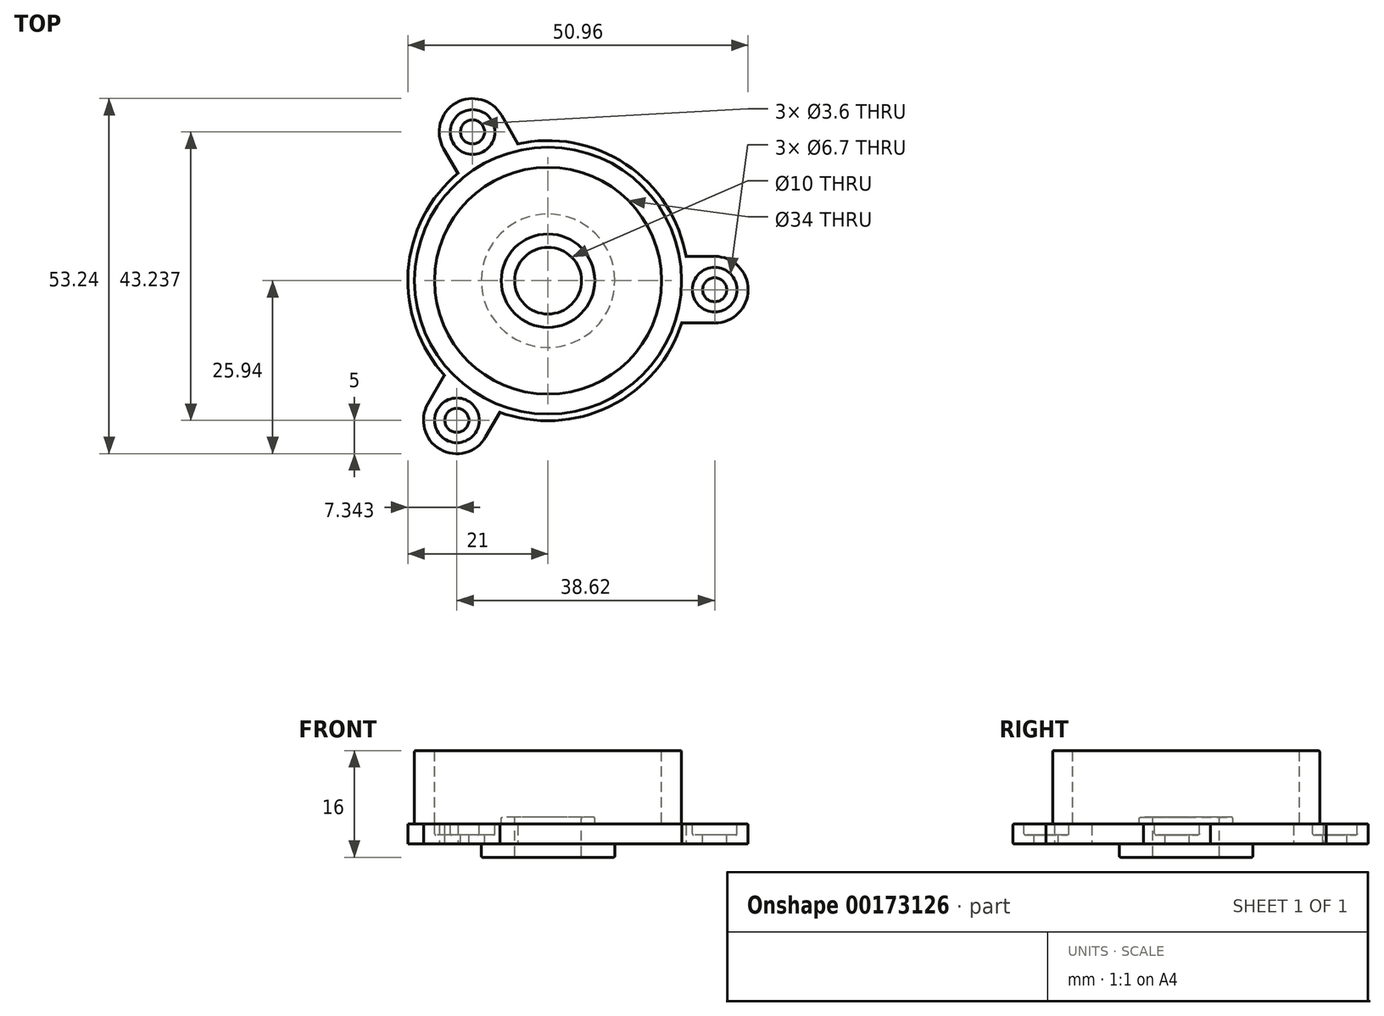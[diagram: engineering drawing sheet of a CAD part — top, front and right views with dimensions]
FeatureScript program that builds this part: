
annotation { "Feature Type Name" : "Feature", "Feature Type Description" : "" }
export const myFeature = defineFeature(function(context is Context, id is Id, definition is map)
    precondition{}
    {
        {
            var Q0;
            Q0=qCreatedBy(makeId("Front.planeOp"),FACE);
            var sketch = newSketch(context, id + "F0", { "sketchPlane" : qUnion([Q0])});
            skLineSegment(sketch, "E0", {"start": v(7, 0) * mm, "end": v(17, 0) * mm});
            skLineSegment(sketch, "E1", {"start": v(17, 0) * mm, "end": v(17, 11) * mm});
            skLineSegment(sketch, "E2", {"start": v(17, 11) * mm, "end": v(20, 11) * mm});
            skLineSegment(sketch, "E3", {"start": v(20, 11) * mm, "end": v(20, 0) * mm});
            skLineSegment(sketch, "E4", {"start": v(20, 0) * mm, "end": v(21, 0) * mm});
            skLineSegment(sketch, "E5", {"start": v(21, 0) * mm, "end": v(21, -3) * mm});
            skLineSegment(sketch, "E6", {"start": v(21, -3) * mm, "end": v(10, -3) * mm});
            skLineSegment(sketch, "E7", {"start": v(10, -3) * mm, "end": v(10, -5) * mm});
            skLineSegment(sketch, "E8", {"start": v(10, -5) * mm, "end": v(5, -5) * mm});
            skLineSegment(sketch, "E9", {"start": v(5, -5) * mm, "end": v(5, 0) * mm});
            skLineSegment(sketch, "E10", {"start": v(5, 0) * mm, "end": v(5, 1) * mm});
            skLineSegment(sketch, "E11", {"start": v(5, 1) * mm, "end": v(7, 1) * mm});
            skLineSegment(sketch, "E12", {"start": v(7, 1) * mm, "end": v(7, 0) * mm});
            skSolve(sketch);
        }
        {
            var Q0;
            Q0=qCreatedBy(makeId("Front.planeOp"),FACE);
            var sketch = newSketch(context, id + "F1", { "sketchPlane" : qUnion([Q0])});
            skLineSegment(sketch, "E13", {"start": v(0, 12.54) * mm, "end": v(0, -18) * mm});
            skSolve(sketch);
        }
        {
            var Q0;
            Q0=makeQuery(id+"F0.imprint","IMPRINT",FACE,{"disambiguationData":[TD([[makeQuery(id+"F0.imprint","IMPRINT",EDGE,{"derivedFrom":sQuery(id+"F0.wireOp",EDGE,"E0")}),-1.0]])]});
            var Q1;
            Q1=sQuery(id+"F1.wireOp",EDGE,"E13");
            revolve(context, id + "F2", {"entities" : qUnion([Q0]), "axis" : qUnion([Q1]), "revolveType" : RevolveType.FULL});
        }
        {
            var Q0;
            Q0=makeQuery(id+"F2.opRevolve","SWEPT_FACE",FACE,{"disambiguationData":[OSD([sQuery(id+"F0.wireOp",EDGE,"E6")])]});
            var sketch = newSketch(context, id + "F3", { "sketchPlane" : qUnion([Q0])});
            skArc(sketch, "E14", {"start": v(24.96, -3.64) * mm, "mid": v(29.96, 1.36) * mm, "end": v(24.96, 6.36) * mm});
            skLineSegment(sketch, "E15", {"start": v(24.96, 6.36) * mm, "end": v(20.01, 6.36) * mm});
            skLineSegment(sketch, "E16", {"start": v(24.96, -3.64) * mm, "end": v(20.68, -3.64) * mm});
            skLineSegment(sketch, "E17.1.0", {"start": v(-17.99, 18.44) * mm, "end": v(-15.51, 14.15) * mm});
            skArc(sketch, "E17.1.1", {"start": v(-9.33, 23.44) * mm, "mid": v(-16.16, 25.27) * mm, "end": v(-17.99, 18.44) * mm});
            skLineSegment(sketch, "E17.1.2", {"start": v(-9.33, 23.44) * mm, "end": v(-7.19, 19.73) * mm});
            skLineSegment(sketch, "E17.2.0", {"start": v(-6.98, -24.8) * mm, "end": v(-4.5, -20.51) * mm});
            skArc(sketch, "E17.2.1", {"start": v(-15.64, -19.8) * mm, "mid": v(-13.8, -26.63) * mm, "end": v(-6.98, -24.8) * mm});
            skLineSegment(sketch, "E17.2.2", {"start": v(-15.64, -19.8) * mm, "end": v(-13.5, -16.09) * mm});
            skPoint(sketch, "E17.center", {"position": v(0, 0) * mm});
            skSolve(sketch);
        }
        {
            var Q0;
            Q0=makeQuery(id+"F3.imprint","IMPRINT",FACE,{"disambiguationData":[TD([[makeQuery(id+"F3.imprint","IMPRINT",EDGE,{"derivedFrom":sQuery(id+"F3.wireOp",EDGE,"E14")}),1.0]])]});
            var Q1;
            {var subQ0=sQuery(id+"F3.wireOp",EDGE,"E17.1.0");Q1=makeQuery(id+"F3.imprint","IMPRINT",FACE,{"disambiguationData":[TD([[makeQuery(id+"F3.imprint","IMPRINT",EDGE,{"derivedFrom":subQ0}),1.0]])]});}
            var Q2;
            {var subQ0=sQuery(id+"F3.wireOp",EDGE,"E17.2.0");Q2=makeQuery(id+"F3.imprint","IMPRINT",FACE,{"disambiguationData":[TD([[makeQuery(id+"F3.imprint","IMPRINT",EDGE,{"derivedFrom":subQ0}),1.0]])]});}
            extrude(context, id + "F4", {"entities" : qUnion([Q0, Q1, Q2]), "operationType" : NewBodyOperationType.ADD, "oppositeDirection" : true, "depth" : 3 * mm});
        }
        {
            var Q0;
            {var subQ0=sQuery(id+"F0.wireOp",EDGE,"E6");var subQ1=sQuery(id+"F0.wireOp",EDGE,"E5");Q0=makeQuery(id+"F4.boolean.opBoolean","MERGE",FACE,{"derivedFrom":[makeQuery(id+"F2.opRevolve","SWEPT_FACE",FACE,{"disambiguationData":[OSD([sQuery(id+"F0.wireOp",EDGE,"E4")])]}),makeQuery(id+"F4.opExtrude","CAP_FACE",FACE,{"disambiguationData":[OSD([subQ1,subQ0,sQuery(id+"F3.wireOp",EDGE,"E14"),sQuery(id+"F3.wireOp",EDGE,"E15"),sQuery(id+"F3.wireOp",EDGE,"E16")])],"isStart":false}),makeQuery(id+"F4.opExtrude","CAP_FACE",FACE,{"disambiguationData":[OSD([subQ1,subQ0,sQuery(id+"F3.wireOp",EDGE,"E17.1.0"),sQuery(id+"F3.wireOp",EDGE,"E17.1.1"),sQuery(id+"F3.wireOp",EDGE,"E17.1.2")])],"isStart":false}),makeQuery(id+"F4.opExtrude","CAP_FACE",FACE,{"disambiguationData":[OSD([subQ1,subQ0,sQuery(id+"F3.wireOp",EDGE,"E17.2.0"),sQuery(id+"F3.wireOp",EDGE,"E17.2.1"),sQuery(id+"F3.wireOp",EDGE,"E17.2.2")])],"isStart":false})]});}
            var sketch = newSketch(context, id + "F5", { "sketchPlane" : qUnion([Q0])});
            skCircle(sketch, "E18", {"center": v(-13.66, -20.94) * mm, "radius": 1.8 * mm});
            skCircle(sketch, "E19.1.0", {"center": v(24.96, -1.36) * mm, "radius": 1.8 * mm});
            skCircle(sketch, "E19.2.0", {"center": v(-11.3, 22.3) * mm, "radius": 1.8 * mm});
            skPoint(sketch, "E19.center", {"position": v(0, 0) * mm});
            skSolve(sketch);
        }
        {
            var Q0;
            Q0=makeQuery(id+"F5.imprint","IMPRINT",FACE,{"disambiguationData":[TD([[makeQuery(id+"F5.imprint","IMPRINT",EDGE,{"derivedFrom":sQuery(id+"F5.wireOp",EDGE,"E18")}),1.0]])]});
            var Q1;
            Q1=makeQuery(id+"F5.imprint","IMPRINT",FACE,{"disambiguationData":[TD([[makeQuery(id+"F5.imprint","IMPRINT",EDGE,{"derivedFrom":sQuery(id+"F5.wireOp",EDGE,"E19.1.0")}),1.0]])]});
            var Q2;
            Q2=makeQuery(id+"F5.imprint","IMPRINT",FACE,{"disambiguationData":[TD([[makeQuery(id+"F5.imprint","IMPRINT",EDGE,{"derivedFrom":sQuery(id+"F5.wireOp",EDGE,"E19.2.0")}),1.0]])]});
            extrude(context, id + "F6", {"entities" : qUnion([Q0, Q1, Q2]), "operationType" : NewBodyOperationType.REMOVE, "endBound" : BoundingType.THROUGH_ALL, "oppositeDirection" : true, "depth" : 25 * mm});
        }
        {
            var Q0;
            {var subQ0=sQuery(id+"F0.wireOp",EDGE,"E6");var subQ1=sQuery(id+"F0.wireOp",EDGE,"E5");Q0=makeQuery(id+"F4.boolean.opBoolean","MERGE",FACE,{"derivedFrom":[makeQuery(id+"F2.opRevolve","SWEPT_FACE",FACE,{"disambiguationData":[OSD([sQuery(id+"F0.wireOp",EDGE,"E4")])]}),makeQuery(id+"F4.opExtrude","CAP_FACE",FACE,{"disambiguationData":[OSD([subQ1,subQ0,sQuery(id+"F3.wireOp",EDGE,"E14"),sQuery(id+"F3.wireOp",EDGE,"E15"),sQuery(id+"F3.wireOp",EDGE,"E16")])],"isStart":false}),makeQuery(id+"F4.opExtrude","CAP_FACE",FACE,{"disambiguationData":[OSD([subQ1,subQ0,sQuery(id+"F3.wireOp",EDGE,"E17.1.0"),sQuery(id+"F3.wireOp",EDGE,"E17.1.1"),sQuery(id+"F3.wireOp",EDGE,"E17.1.2")])],"isStart":false}),makeQuery(id+"F4.opExtrude","CAP_FACE",FACE,{"disambiguationData":[OSD([subQ1,subQ0,sQuery(id+"F3.wireOp",EDGE,"E17.2.0"),sQuery(id+"F3.wireOp",EDGE,"E17.2.1"),sQuery(id+"F3.wireOp",EDGE,"E17.2.2")])],"isStart":false})]});}
            var sketch = newSketch(context, id + "F7", { "sketchPlane" : qUnion([Q0])});
            skCircle(sketch, "E20", {"center": v(-13.66, -20.94) * mm, "radius": 3.35 * mm});
            skCircle(sketch, "E21.1.0", {"center": v(24.96, -1.36) * mm, "radius": 3.35 * mm});
            skCircle(sketch, "E21.2.0", {"center": v(-11.3, 22.3) * mm, "radius": 3.35 * mm});
            skPoint(sketch, "E21.center", {"position": v(0, 0) * mm});
            skSolve(sketch);
        }
        {
            var Q0;
            Q0=makeQuery(id+"F7.imprint","IMPRINT",FACE,{"disambiguationData":[TD([[makeQuery(id+"F7.imprint","IMPRINT",EDGE,{"derivedFrom":sQuery(id+"F7.wireOp",EDGE,"E20")}),1.0]])]});
            var Q1;
            Q1=makeQuery(id+"F7.imprint","IMPRINT",FACE,{"disambiguationData":[TD([[makeQuery(id+"F7.imprint","IMPRINT",EDGE,{"derivedFrom":sQuery(id+"F7.wireOp",EDGE,"E21.1.0")}),1.0]])]});
            var Q2;
            Q2=makeQuery(id+"F7.imprint","IMPRINT",FACE,{"disambiguationData":[TD([[makeQuery(id+"F7.imprint","IMPRINT",EDGE,{"derivedFrom":sQuery(id+"F7.wireOp",EDGE,"E21.2.0")}),1.0]])]});
            extrude(context, id + "F8", {"entities" : qUnion([Q0, Q1, Q2]), "operationType" : NewBodyOperationType.REMOVE, "oppositeDirection" : true, "depth" : 1.65 * mm});
        }
        {
            var Q0;
            Q0=makeQuery(id+"F2.opRevolve","SWEPT_EDGE",EDGE,{"disambiguationData":[OSD([sQuery(id+"F0.wireOp",EDGE,"E1"),sQuery(id+"F0.wireOp",EDGE,"E2")])]});
            var Q1;
            Q1=makeQuery(id+"F2.opRevolve","SWEPT_EDGE",EDGE,{"disambiguationData":[OSD([sQuery(id+"F0.wireOp",EDGE,"E2"),sQuery(id+"F0.wireOp",EDGE,"E3")])]});
            var Q2;
            Q2=makeQuery(id+"F2.opRevolve","SWEPT_EDGE",EDGE,{"disambiguationData":[OSD([sQuery(id+"F0.wireOp",EDGE,"E0"),sQuery(id+"F0.wireOp",EDGE,"E1")])]});
            var Q3;
            Q3=makeQuery(id+"F2.opRevolve","SWEPT_EDGE",EDGE,{"disambiguationData":[OSD([sQuery(id+"F0.wireOp",EDGE,"E11"),sQuery(id+"F0.wireOp",EDGE,"E12")])]});
            var Q4;
            Q4=makeQuery(id+"F2.opRevolve","SWEPT_EDGE",EDGE,{"disambiguationData":[OSD([sQuery(id+"F0.wireOp",EDGE,"E10"),sQuery(id+"F0.wireOp",EDGE,"E11")])]});
            var Q5;
            Q5=makeQuery(id+"F2.opRevolve","SWEPT_EDGE",EDGE,{"disambiguationData":[OSD([sQuery(id+"F0.wireOp",EDGE,"E0"),sQuery(id+"F0.wireOp",EDGE,"E12")])]});
            var Q6;
            {var subQ0=sQuery(id+"F3.wireOp",EDGE,"E16");var subQ1=sQuery(id+"F0.wireOp",EDGE,"E4");var subQ3=sQuery(id+"F0.wireOp",EDGE,"E5");Q6=makeQuery(id+"F4.boolean.opBoolean","SPLIT",EDGE,{"disambiguationData":[TD([makeQuery(id+"F4.opExtrude","SWEPT_FACE",FACE,{"disambiguationData":[OSD([subQ0])]})])],"derivedFrom":makeQuery(id+"F2.opRevolve","SWEPT_EDGE",EDGE,{"disambiguationData":[OSD([subQ1,subQ3])]})});}
            var Q7;
            Q7=makeQuery(id+"F2.opRevolve","SWEPT_EDGE",EDGE,{"disambiguationData":[OSD([sQuery(id+"F0.wireOp",EDGE,"E3"),sQuery(id+"F0.wireOp",EDGE,"E4")])]});
            var Q8;
            Q8=makeQuery(id+"F4.opExtrude","CAP_EDGE",EDGE,{"disambiguationData":[OSD([sQuery(id+"F3.wireOp",EDGE,"E17.2.0")])],"isStart":false});
            var Q9;
            Q9=makeQuery(id+"F4.opExtrude","CAP_EDGE",EDGE,{"disambiguationData":[OSD([sQuery(id+"F3.wireOp",EDGE,"E17.2.1")])],"isStart":false});
            var Q10;
            Q10=makeQuery(id+"F4.opExtrude","CAP_EDGE",EDGE,{"disambiguationData":[OSD([sQuery(id+"F3.wireOp",EDGE,"E17.2.2")])],"isStart":false});
            var Q11;
            Q11=makeQuery(id+"F8.boolean.opBoolean","COPY",EDGE,{"derivedFrom":makeQuery(id+"F8.opExtrude","CAP_EDGE",EDGE,{"disambiguationData":[OSD([sQuery(id+"F7.wireOp",EDGE,"E21.2.0")])],"isStart":true})});
            var Q12;
            Q12=makeQuery(id+"F8.boolean.opBoolean","COPY",EDGE,{"derivedFrom":makeQuery(id+"F8.opExtrude","CAP_EDGE",EDGE,{"disambiguationData":[OSD([sQuery(id+"F7.wireOp",EDGE,"E21.2.0")])],"isStart":false})});
            var Q13;
            Q13=makeQuery(id+"F8.boolean.opBoolean","COPY",EDGE,{"derivedFrom":makeQuery(id+"F8.opExtrude","CAP_EDGE",EDGE,{"disambiguationData":[OSD([sQuery(id+"F5.wireOp",EDGE,"E19.2.0")])],"isStart":false})});
            var Q14;
            {var subQ0=sQuery(id+"F0.wireOp",EDGE,"E6");var subQ1=sQuery(id+"F0.wireOp",EDGE,"E5");Q14=makeQuery(id+"F6.boolean.opBoolean","INTERSECT",EDGE,{"derivedFrom":[makeQuery(id+"F4.boolean.opBoolean","MERGE",FACE,{"derivedFrom":[makeQuery(id+"F2.opRevolve","SWEPT_FACE",FACE,{"disambiguationData":[OSD([subQ0])]}),makeQuery(id+"F4.opExtrude","CAP_FACE",FACE,{"disambiguationData":[OSD([subQ1,subQ0,sQuery(id+"F3.wireOp",EDGE,"E14"),sQuery(id+"F3.wireOp",EDGE,"E15"),sQuery(id+"F3.wireOp",EDGE,"E16")])],"isStart":true}),makeQuery(id+"F4.opExtrude","CAP_FACE",FACE,{"disambiguationData":[OSD([subQ1,subQ0,sQuery(id+"F3.wireOp",EDGE,"E17.1.0"),sQuery(id+"F3.wireOp",EDGE,"E17.1.1"),sQuery(id+"F3.wireOp",EDGE,"E17.1.2")])],"isStart":true}),makeQuery(id+"F4.opExtrude","CAP_FACE",FACE,{"disambiguationData":[OSD([subQ1,subQ0,sQuery(id+"F3.wireOp",EDGE,"E17.2.0"),sQuery(id+"F3.wireOp",EDGE,"E17.2.1"),sQuery(id+"F3.wireOp",EDGE,"E17.2.2")])],"isStart":true})]}),makeQuery(id+"F6.opExtrude","SWEPT_FACE",FACE,{"disambiguationData":[OSD([sQuery(id+"F5.wireOp",EDGE,"E19.2.0")])]})]});}
            var Q15;
            Q15=makeQuery(id+"F4.opExtrude","CAP_EDGE",EDGE,{"disambiguationData":[OSD([sQuery(id+"F3.wireOp",EDGE,"E17.2.0")])],"isStart":true});
            var Q16;
            Q16=makeQuery(id+"F4.opExtrude","CAP_EDGE",EDGE,{"disambiguationData":[OSD([sQuery(id+"F3.wireOp",EDGE,"E17.2.1")])],"isStart":true});
            var Q17;
            Q17=makeQuery(id+"F4.opExtrude","CAP_EDGE",EDGE,{"disambiguationData":[OSD([sQuery(id+"F3.wireOp",EDGE,"E17.2.1")])],"isStart":true});
            var Q18;
            {var subQ0=sQuery(id+"F3.wireOp",EDGE,"E16");var subQ1=sQuery(id+"F0.wireOp",EDGE,"E6");var subQ2=sQuery(id+"F0.wireOp",EDGE,"E5");Q18=makeQuery(id+"F4.boolean.opBoolean","SPLIT",EDGE,{"disambiguationData":[TD([makeQuery(id+"F4.opExtrude","SWEPT_FACE",FACE,{"disambiguationData":[OSD([subQ0])]})])],"derivedFrom":makeQuery(id+"F2.opRevolve","SWEPT_EDGE",EDGE,{"disambiguationData":[OSD([subQ2,subQ1])]})});}
            var Q19;
            Q19=makeQuery(id+"F4.opExtrude","CAP_EDGE",EDGE,{"disambiguationData":[OSD([sQuery(id+"F3.wireOp",EDGE,"E16")])],"isStart":false});
            var Q20;
            Q20=makeQuery(id+"F8.boolean.opBoolean","COPY",EDGE,{"derivedFrom":makeQuery(id+"F8.opExtrude","CAP_EDGE",EDGE,{"disambiguationData":[OSD([sQuery(id+"F7.wireOp",EDGE,"E21.1.0")])],"isStart":true})});
            var Q21;
            Q21=makeQuery(id+"F8.boolean.opBoolean","COPY",EDGE,{"derivedFrom":makeQuery(id+"F8.opExtrude","CAP_EDGE",EDGE,{"disambiguationData":[OSD([sQuery(id+"F7.wireOp",EDGE,"E21.1.0")])],"isStart":false})});
            var Q22;
            {var subQ0=sQuery(id+"F0.wireOp",EDGE,"E6");var subQ1=sQuery(id+"F0.wireOp",EDGE,"E5");Q22=makeQuery(id+"F6.boolean.opBoolean","INTERSECT",EDGE,{"derivedFrom":[makeQuery(id+"F4.boolean.opBoolean","MERGE",FACE,{"derivedFrom":[makeQuery(id+"F2.opRevolve","SWEPT_FACE",FACE,{"disambiguationData":[OSD([subQ0])]}),makeQuery(id+"F4.opExtrude","CAP_FACE",FACE,{"disambiguationData":[OSD([subQ1,subQ0,sQuery(id+"F3.wireOp",EDGE,"E14"),sQuery(id+"F3.wireOp",EDGE,"E15"),sQuery(id+"F3.wireOp",EDGE,"E16")])],"isStart":true}),makeQuery(id+"F4.opExtrude","CAP_FACE",FACE,{"disambiguationData":[OSD([subQ1,subQ0,sQuery(id+"F3.wireOp",EDGE,"E17.1.0"),sQuery(id+"F3.wireOp",EDGE,"E17.1.1"),sQuery(id+"F3.wireOp",EDGE,"E17.1.2")])],"isStart":true}),makeQuery(id+"F4.opExtrude","CAP_FACE",FACE,{"disambiguationData":[OSD([subQ1,subQ0,sQuery(id+"F3.wireOp",EDGE,"E17.2.0"),sQuery(id+"F3.wireOp",EDGE,"E17.2.1"),sQuery(id+"F3.wireOp",EDGE,"E17.2.2")])],"isStart":true})]}),makeQuery(id+"F6.opExtrude","SWEPT_FACE",FACE,{"disambiguationData":[OSD([sQuery(id+"F5.wireOp",EDGE,"E19.1.0")])]})]});}
            var Q23;
            Q23=makeQuery(id+"F8.boolean.opBoolean","COPY",EDGE,{"derivedFrom":makeQuery(id+"F8.opExtrude","CAP_EDGE",EDGE,{"disambiguationData":[OSD([sQuery(id+"F5.wireOp",EDGE,"E19.1.0")])],"isStart":false})});
            var Q24;
            Q24=makeQuery(id+"F4.opExtrude","CAP_EDGE",EDGE,{"disambiguationData":[OSD([sQuery(id+"F3.wireOp",EDGE,"E15")])],"isStart":false});
            var Q25;
            Q25=makeQuery(id+"F4.opExtrude","CAP_EDGE",EDGE,{"disambiguationData":[OSD([sQuery(id+"F3.wireOp",EDGE,"E14")])],"isStart":false});
            var Q26;
            {var subQ0=sQuery(id+"F3.wireOp",EDGE,"E15");var subQ3=sQuery(id+"F0.wireOp",EDGE,"E5");var subQ4=sQuery(id+"F0.wireOp",EDGE,"E4");Q26=makeQuery(id+"F4.boolean.opBoolean","SPLIT",EDGE,{"disambiguationData":[TD([makeQuery(id+"F4.opExtrude","SWEPT_FACE",FACE,{"disambiguationData":[OSD([subQ0])]})])],"derivedFrom":makeQuery(id+"F2.opRevolve","SWEPT_EDGE",EDGE,{"disambiguationData":[OSD([subQ4,subQ3])]})});}
            var Q27;
            Q27=makeQuery(id+"F4.opExtrude","CAP_EDGE",EDGE,{"disambiguationData":[OSD([sQuery(id+"F3.wireOp",EDGE,"E17.1.2")])],"isStart":false});
            var Q28;
            {var subQ0=sQuery(id+"F3.wireOp",EDGE,"E15");var subQ2=sQuery(id+"F0.wireOp",EDGE,"E6");var subQ3=sQuery(id+"F0.wireOp",EDGE,"E5");Q28=makeQuery(id+"F4.boolean.opBoolean","SPLIT",EDGE,{"disambiguationData":[TD([makeQuery(id+"F4.opExtrude","SWEPT_FACE",FACE,{"disambiguationData":[OSD([subQ0])]})])],"derivedFrom":makeQuery(id+"F2.opRevolve","SWEPT_EDGE",EDGE,{"disambiguationData":[OSD([subQ3,subQ2])]})});}
            var Q29;
            Q29=makeQuery(id+"F4.opExtrude","SWEPT_EDGE",EDGE,{"disambiguationData":[OSD([sQuery(id+"F0.wireOp",EDGE,"E5"),sQuery(id+"F0.wireOp",EDGE,"E6"),sQuery(id+"F3.wireOp",EDGE,"E17.1.2")])]});
            var Q30;
            Q30=makeQuery(id+"F4.opExtrude","SWEPT_EDGE",EDGE,{"disambiguationData":[OSD([sQuery(id+"F0.wireOp",EDGE,"E5"),sQuery(id+"F0.wireOp",EDGE,"E6"),sQuery(id+"F3.wireOp",EDGE,"E15")])]});
            var Q31;
            Q31=makeQuery(id+"F4.opExtrude","CAP_EDGE",EDGE,{"disambiguationData":[OSD([sQuery(id+"F3.wireOp",EDGE,"E15")])],"isStart":true});
            var Q32;
            Q32=makeQuery(id+"F4.opExtrude","CAP_EDGE",EDGE,{"disambiguationData":[OSD([sQuery(id+"F3.wireOp",EDGE,"E14")])],"isStart":true});
            var Q33;
            Q33=makeQuery(id+"F4.opExtrude","CAP_EDGE",EDGE,{"disambiguationData":[OSD([sQuery(id+"F3.wireOp",EDGE,"E17.1.2")])],"isStart":true});
            var Q34;
            Q34=makeQuery(id+"F4.opExtrude","CAP_EDGE",EDGE,{"disambiguationData":[OSD([sQuery(id+"F3.wireOp",EDGE,"E17.1.1")])],"isStart":true});
            var Q35;
            Q35=makeQuery(id+"F8.boolean.opBoolean","COPY",EDGE,{"derivedFrom":makeQuery(id+"F8.opExtrude","CAP_EDGE",EDGE,{"disambiguationData":[OSD([sQuery(id+"F7.wireOp",EDGE,"E20")])],"isStart":true})});
            var Q36;
            Q36=makeQuery(id+"F8.boolean.opBoolean","COPY",EDGE,{"derivedFrom":makeQuery(id+"F8.opExtrude","CAP_EDGE",EDGE,{"disambiguationData":[OSD([sQuery(id+"F7.wireOp",EDGE,"E20")])],"isStart":false})});
            var Q37;
            Q37=makeQuery(id+"F8.boolean.opBoolean","COPY",EDGE,{"derivedFrom":makeQuery(id+"F8.opExtrude","CAP_EDGE",EDGE,{"disambiguationData":[OSD([sQuery(id+"F5.wireOp",EDGE,"E18")])],"isStart":false})});
            var Q38;
            Q38=makeQuery(id+"F4.opExtrude","CAP_EDGE",EDGE,{"disambiguationData":[OSD([sQuery(id+"F3.wireOp",EDGE,"E17.1.1")])],"isStart":false});
            var Q39;
            {var subQ1=sQuery(id+"F0.wireOp",EDGE,"E5");var subQ2=sQuery(id+"F3.wireOp",EDGE,"E17.1.0");var subQ3=sQuery(id+"F0.wireOp",EDGE,"E4");Q39=makeQuery(id+"F4.boolean.opBoolean","SPLIT",EDGE,{"disambiguationData":[TD([makeQuery(id+"F4.opExtrude","SWEPT_FACE",FACE,{"disambiguationData":[OSD([subQ2])]})])],"derivedFrom":makeQuery(id+"F2.opRevolve","SWEPT_EDGE",EDGE,{"disambiguationData":[OSD([subQ3,subQ1])]})});}
            var Q40;
            Q40=makeQuery(id+"F4.opExtrude","CAP_EDGE",EDGE,{"disambiguationData":[OSD([sQuery(id+"F3.wireOp",EDGE,"E17.1.0")])],"isStart":false});
            var Q41;
            Q41=makeQuery(id+"F4.opExtrude","CAP_EDGE",EDGE,{"disambiguationData":[OSD([sQuery(id+"F3.wireOp",EDGE,"E17.1.0")])],"isStart":true});
            var Q42;
            {var subQ0=sQuery(id+"F0.wireOp",EDGE,"E6");var subQ1=sQuery(id+"F3.wireOp",EDGE,"E17.1.0");var subQ2=sQuery(id+"F0.wireOp",EDGE,"E5");Q42=makeQuery(id+"F4.boolean.opBoolean","SPLIT",EDGE,{"disambiguationData":[TD([makeQuery(id+"F4.opExtrude","SWEPT_FACE",FACE,{"disambiguationData":[OSD([subQ1])]})])],"derivedFrom":makeQuery(id+"F2.opRevolve","SWEPT_EDGE",EDGE,{"disambiguationData":[OSD([subQ2,subQ0])]})});}
            var Q43;
            Q43=makeQuery(id+"F4.opExtrude","CAP_EDGE",EDGE,{"disambiguationData":[OSD([sQuery(id+"F3.wireOp",EDGE,"E16")])],"isStart":true});
            var Q44;
            Q44=makeQuery(id+"F2.opRevolve","SWEPT_EDGE",EDGE,{"disambiguationData":[OSD([sQuery(id+"F0.wireOp",EDGE,"E8"),sQuery(id+"F0.wireOp",EDGE,"E9")])]});
            var Q45;
            Q45=makeQuery(id+"F2.opRevolve","SWEPT_EDGE",EDGE,{"disambiguationData":[OSD([sQuery(id+"F0.wireOp",EDGE,"E7"),sQuery(id+"F0.wireOp",EDGE,"E8")])]});
            var Q46;
            Q46=makeQuery(id+"F2.opRevolve","SWEPT_EDGE",EDGE,{"disambiguationData":[OSD([sQuery(id+"F0.wireOp",EDGE,"E6"),sQuery(id+"F0.wireOp",EDGE,"E7")])]});
            var Q47;
            Q47=makeQuery(id+"F2.opRevolve","SWEPT_EDGE",EDGE,{"disambiguationData":[OSD([sQuery(id+"F0.wireOp",EDGE,"E8"),sQuery(id+"F0.wireOp",EDGE,"E9")])]});
            var Q48;
            Q48=makeQuery(id+"F4.opExtrude","CAP_EDGE",EDGE,{"disambiguationData":[OSD([sQuery(id+"F3.wireOp",EDGE,"E17.2.2")])],"isStart":true});
            var Q49;
            Q49=makeQuery(id+"F4.opExtrude","SWEPT_EDGE",EDGE,{"disambiguationData":[OSD([sQuery(id+"F0.wireOp",EDGE,"E5"),sQuery(id+"F0.wireOp",EDGE,"E6"),sQuery(id+"F3.wireOp",EDGE,"E17.1.0")])]});
            var Q50;
            Q50=makeQuery(id+"F4.opExtrude","SWEPT_EDGE",EDGE,{"disambiguationData":[OSD([sQuery(id+"F0.wireOp",EDGE,"E5"),sQuery(id+"F0.wireOp",EDGE,"E6"),sQuery(id+"F3.wireOp",EDGE,"E17.2.2")])]});
            var Q51;
            Q51=makeQuery(id+"F4.opExtrude","SWEPT_EDGE",EDGE,{"disambiguationData":[OSD([sQuery(id+"F3.wireOp",EDGE,"E17.1.0"),sQuery(id+"F3.wireOp",EDGE,"E17.1.1")])]});
            var Q52;
            Q52=makeQuery(id+"F4.opExtrude","SWEPT_EDGE",EDGE,{"disambiguationData":[OSD([sQuery(id+"F0.wireOp",EDGE,"E5"),sQuery(id+"F0.wireOp",EDGE,"E6"),sQuery(id+"F3.wireOp",EDGE,"E16")])]});
            fillet(context, id + "F9", {"entities" : qUnion([Q0, Q1, Q2, Q3, Q4, Q5, Q6, Q7, Q8, Q9, Q10, Q11, Q12, Q13, Q14, Q15, Q16, Q17, Q18, Q19, Q20, Q21, Q22, Q23, Q24, Q25, Q26, Q27, Q28, Q29, Q30, Q31, Q32, Q33, Q34, Q35, Q36, Q37, Q38, Q39, Q40, Q41, Q42, Q43, Q44, Q45, Q46, Q47, Q48, Q49, Q50, Q51, Q52]), "radius" : .2 * mm, "tangentPropagation" : true, "allowEdgeOverflow" : false});
        }
    });
